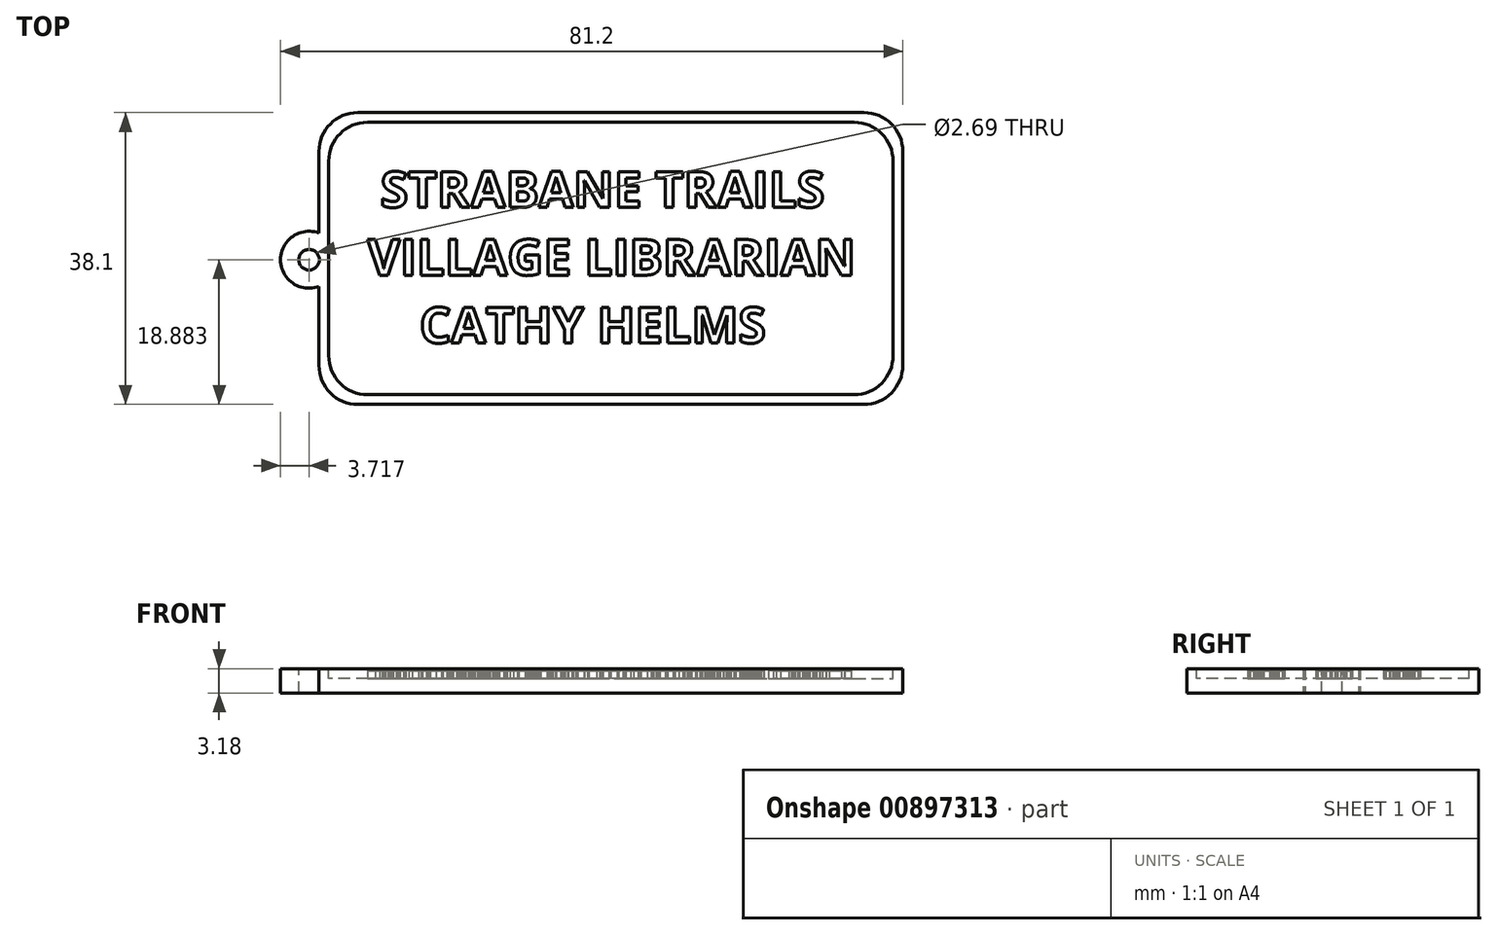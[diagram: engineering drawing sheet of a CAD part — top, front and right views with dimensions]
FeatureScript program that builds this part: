
annotation { "Feature Type Name" : "Feature", "Feature Type Description" : "" }
export const myFeature = defineFeature(function(context is Context, id is Id, definition is map)
    precondition{}
    {
        {
            var Q0;
            Q0=qCreatedBy(makeId("Top.planeOp"),FACE);
            var sketch = newSketch(context, id + "F0", { "sketchPlane" : qUnion([Q0])});
            skLineSegment(sketch, "E0.right", {"start": v(59.03, 19.05) * mm, "end": v(59.03, -19.05) * mm});
            skArc(sketch, "E1", {"start": v(-17.17, 3.32) * mm, "mid": v(-22.17, -0.17) * mm, "end": v(-17.17, -3.66) * mm});
            skPoint(sketch, "E1.centerSnap0", {"position": v(-22.6, -0.17) * mm});
            skLineSegment(sketch, "E2", {"start": v(-17.17, 3.32) * mm, "end": v(-17.17, 19.05) * mm});
            skLineSegment(sketch, "E3", {"start": v(-17.17, -3.66) * mm, "end": v(-17.17, -19.05) * mm});
            skPoint(sketch, "E4.orphan", {"position": v(-22.6, 14.34) * mm});
            skPoint(sketch, "E5.orphan", {"position": v(-22.6, -14.68) * mm});
            skLineSegment(sketch, "E6", {"start": v(-17.17, 19.05) * mm, "end": v(59.03, 19.05) * mm});
            skLineSegment(sketch, "E7", {"start": v(-17.17, -19.05) * mm, "end": v(59.03, -19.05) * mm});
            skSolve(sketch);
        }
        {
            var Q0;
            Q0=makeQuery(id+"F0.imprint","IMPRINT",FACE,{"disambiguationData":[TD([[makeQuery(id+"F0.imprint","IMPRINT",EDGE,{"derivedFrom":sQuery(id+"F0.wireOp",EDGE,"E0.right")}),-1.0]])]});
            extrude(context, id + "F1", {"entities" : qUnion([Q0]), "endBound" : BoundingType.SYMMETRIC, "depth" : 3.17 * mm, "offsetDistance" : 25.4 * mm});
        }
        {
            var Q0;
            {var subQ0=sQuery(id+"F0.wireOp",EDGE,"E1");var subQ1=sQuery(id+"F0.wireOp",EDGE,"E3");var subQ2=sQuery(id+"F0.wireOp",EDGE,"E0.right");var subQ3=sQuery(id+"F0.wireOp",EDGE,"E6");var subQ4=sQuery(id+"F0.wireOp",EDGE,"E7");var subQ5=sQuery(id+"F0.wireOp",EDGE,"E2");Q0=makeQuery(id+"FPCTxZ15ulyRdRa_1.boolean.opBoolean","SPLIT",FACE,{"disambiguationData":[TD([makeQuery(id+"F1.opExtrude","SWEPT_FACE",FACE,{"disambiguationData":[OSD([subQ2])]})])],"derivedFrom":makeQuery(id+"F1.opExtrude","CAP_FACE",FACE,{"disambiguationData":[OSD([subQ2,subQ0,subQ5,subQ1,subQ3,subQ4])],"isStart":false})});}
            var sketch = newSketch(context, id + "F2", { "sketchPlane" : qUnion([Q0])});
            skCircle(sketch, "E8", {"center": v(-18.45, -0.17) * mm, "radius": 1.35 * mm});
            skSolve(sketch);
        }
        {
            var Q0;
            Q0=makeQuery(id+"F2.imprint","IMPRINT",FACE,{"disambiguationData":[TD([[makeQuery(id+"F2.imprint","IMPRINT",EDGE,{"derivedFrom":sQuery(id+"F2.wireOp",EDGE,"E8")}),1.0]])]});
            extrude(context, id + "F3", {"entities" : qUnion([Q0]), "operationType" : NewBodyOperationType.REMOVE, "endBound" : BoundingType.THROUGH_ALL, "oppositeDirection" : true, "depth" : 25.4 * mm, "offsetDistance" : 25.4 * mm});
        }
        {
            var Q0;
            Q0=makeQuery(id+"F1.opExtrude","CAP_FACE",FACE,{"disambiguationData":[OSD([sQuery(id+"F0.wireOp",EDGE,"E0.right"),sQuery(id+"F0.wireOp",EDGE,"E1"),sQuery(id+"F0.wireOp",EDGE,"E2"),sQuery(id+"F0.wireOp",EDGE,"E3"),sQuery(id+"F0.wireOp",EDGE,"E6"),sQuery(id+"F0.wireOp",EDGE,"E7")])],"isStart":false});
            var sketch = newSketch(context, id + "F4", { "sketchPlane" : qUnion([Q0])});
            skLineSegment(sketch, "E9.bottom", {"start": v(-15.9, 17.78) * mm, "end": v(57.76, 17.78) * mm});
            skLineSegment(sketch, "E9.top", {"start": v(-15.9, -17.78) * mm, "end": v(57.76, -17.78) * mm});
            skLineSegment(sketch, "E9.left", {"start": v(-15.9, 17.78) * mm, "end": v(-15.9, -17.78) * mm});
            skLineSegment(sketch, "E9.right", {"start": v(57.76, 17.78) * mm, "end": v(57.76, -17.78) * mm});
            skSolve(sketch);
        }
        {
            var Q0;
            Q0=makeQuery(id+"F4.imprint","IMPRINT",FACE,{"disambiguationData":[TD([[makeQuery(id+"F4.imprint","IMPRINT",EDGE,{"derivedFrom":sQuery(id+"F4.wireOp",EDGE,"E9.bottom")}),-1.0]])]});
            extrude(context, id + "F5", {"entities" : qUnion([Q0]), "operationType" : NewBodyOperationType.REMOVE, "oppositeDirection" : true, "depth" : 1.27 * mm, "offsetDistance" : 25.4 * mm});
        }
        {
            var Q0;
            Q0=makeQuery(id+"F5.boolean.opBoolean","COPY",FACE,{"derivedFrom":makeQuery(id+"F5.opExtrude","CAP_FACE",FACE,{"disambiguationData":[OSD([sQuery(id+"F4.wireOp",EDGE,"E9.bottom"),sQuery(id+"F4.wireOp",EDGE,"E9.top"),sQuery(id+"F4.wireOp",EDGE,"E9.left"),sQuery(id+"F4.wireOp",EDGE,"E9.right")])],"isStart":false})});
            var sketch = newSketch(context, id + "F6", { "sketchPlane" : qUnion([Q0])});
            skText(sketch, "E10", { "text": " STRABANE TRAILS \nVILLAGE LIBRARIAN\n    CATHY HELMS", "fontName": "OpenSans-Bold.ttf"});
            const initialGuessF6  = {"E10": [-0.01082, 0.00668, 1, 0, 0.00469]};
            skSetInitialGuess(sketch, initialGuessF6);
            skSolve(sketch);
        }
        {
            var Q0;
            Q0 = qSketchRegion(id + "F6", true);
            extrude(context, id + "F7", {"entities" : qUnion([Q0]), "operationType" : NewBodyOperationType.ADD, "depth" : 1.02 * mm, "offsetDistance" : 25.4 * mm});
        }
        {
            var Q0;
            Q0=makeQuery(id+"F1.opExtrude","SWEPT_EDGE",EDGE,{"disambiguationData":[OSD([sQuery(id+"F0.wireOp",EDGE,"E2"),sQuery(id+"F0.wireOp",EDGE,"E6")])]});
            var Q1;
            Q1=makeQuery(id+"F1.opExtrude","SWEPT_EDGE",EDGE,{"disambiguationData":[OSD([sQuery(id+"F0.wireOp",EDGE,"E0.right"),sQuery(id+"F0.wireOp",EDGE,"E6")])]});
            var Q2;
            Q2=makeQuery(id+"F1.opExtrude","SWEPT_EDGE",EDGE,{"disambiguationData":[OSD([sQuery(id+"F0.wireOp",EDGE,"E3"),sQuery(id+"F0.wireOp",EDGE,"E7")])]});
            var Q3;
            Q3=makeQuery(id+"F1.opExtrude","SWEPT_EDGE",EDGE,{"disambiguationData":[OSD([sQuery(id+"F0.wireOp",EDGE,"E0.right"),sQuery(id+"F0.wireOp",EDGE,"E7")])]});
            var Q4;
            Q4=makeQuery(id+"F5.boolean.opBoolean","COPY",EDGE,{"derivedFrom":makeQuery(id+"F5.opExtrude","SWEPT_EDGE",EDGE,{"disambiguationData":[OSD([sQuery(id+"F4.wireOp",EDGE,"E9.top"),sQuery(id+"F4.wireOp",EDGE,"E9.right")])]})});
            var Q5;
            Q5=makeQuery(id+"F5.boolean.opBoolean","COPY",EDGE,{"derivedFrom":makeQuery(id+"F5.opExtrude","SWEPT_EDGE",EDGE,{"disambiguationData":[OSD([sQuery(id+"F4.wireOp",EDGE,"E9.top"),sQuery(id+"F4.wireOp",EDGE,"E9.left")])]})});
            var Q6;
            Q6=makeQuery(id+"F5.boolean.opBoolean","COPY",EDGE,{"derivedFrom":makeQuery(id+"F5.opExtrude","SWEPT_EDGE",EDGE,{"disambiguationData":[OSD([sQuery(id+"F4.wireOp",EDGE,"E9.bottom"),sQuery(id+"F4.wireOp",EDGE,"E9.right")])]})});
            var Q7;
            Q7=makeQuery(id+"F5.boolean.opBoolean","COPY",EDGE,{"derivedFrom":makeQuery(id+"F5.opExtrude","SWEPT_EDGE",EDGE,{"disambiguationData":[OSD([sQuery(id+"F4.wireOp",EDGE,"E9.bottom"),sQuery(id+"F4.wireOp",EDGE,"E9.left")])]})});
            fillet(context, id + "F8", {"entities" : qUnion([Q0, Q1, Q2, Q3, Q4, Q5, Q6, Q7]), "tangentPropagation" : true, "radius" : 5.08 * mm, "defaultsChanged" : true, "vertexSettings" : [], "allowEdgeOverflow" : false});
        }
    });
